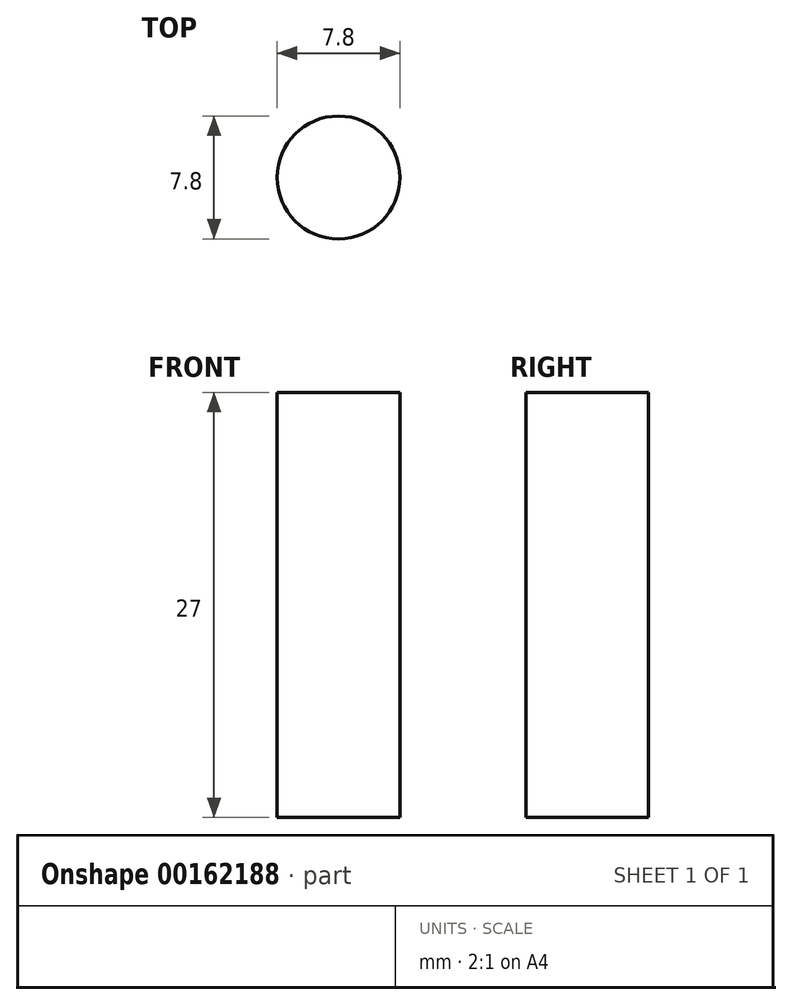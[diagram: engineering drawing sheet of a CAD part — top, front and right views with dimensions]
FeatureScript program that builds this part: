
annotation { "Feature Type Name" : "Feature", "Feature Type Description" : "" }
export const myFeature = defineFeature(function(context is Context, id is Id, definition is map)
    precondition{}
    {
        {
            var Q0;
            Q0=qCreatedBy(makeId("Top.planeOp"),FACE);
            var sketch = newSketch(context, id + "F0", { "sketchPlane" : qUnion([Q0])});
            skCircle(sketch, "E0", {"center": v(0, 0) * mm, "radius": 3.9 * mm});
            skSolve(sketch);
        }
        {
            var Q0;
            Q0=makeQuery(id+"F0.imprint","IMPRINT",FACE,{"disambiguationData":[TD([[makeQuery(id+"F0.imprint","IMPRINT",EDGE,{"derivedFrom":sQuery(id+"F0.wireOp",EDGE,"E0")}),1.0]])]});
            extrude(context, id + "F1", {"entities" : qUnion([Q0]), "depth" : 27 * mm, "offsetDistance" : 25 * mm});
        }
    });
